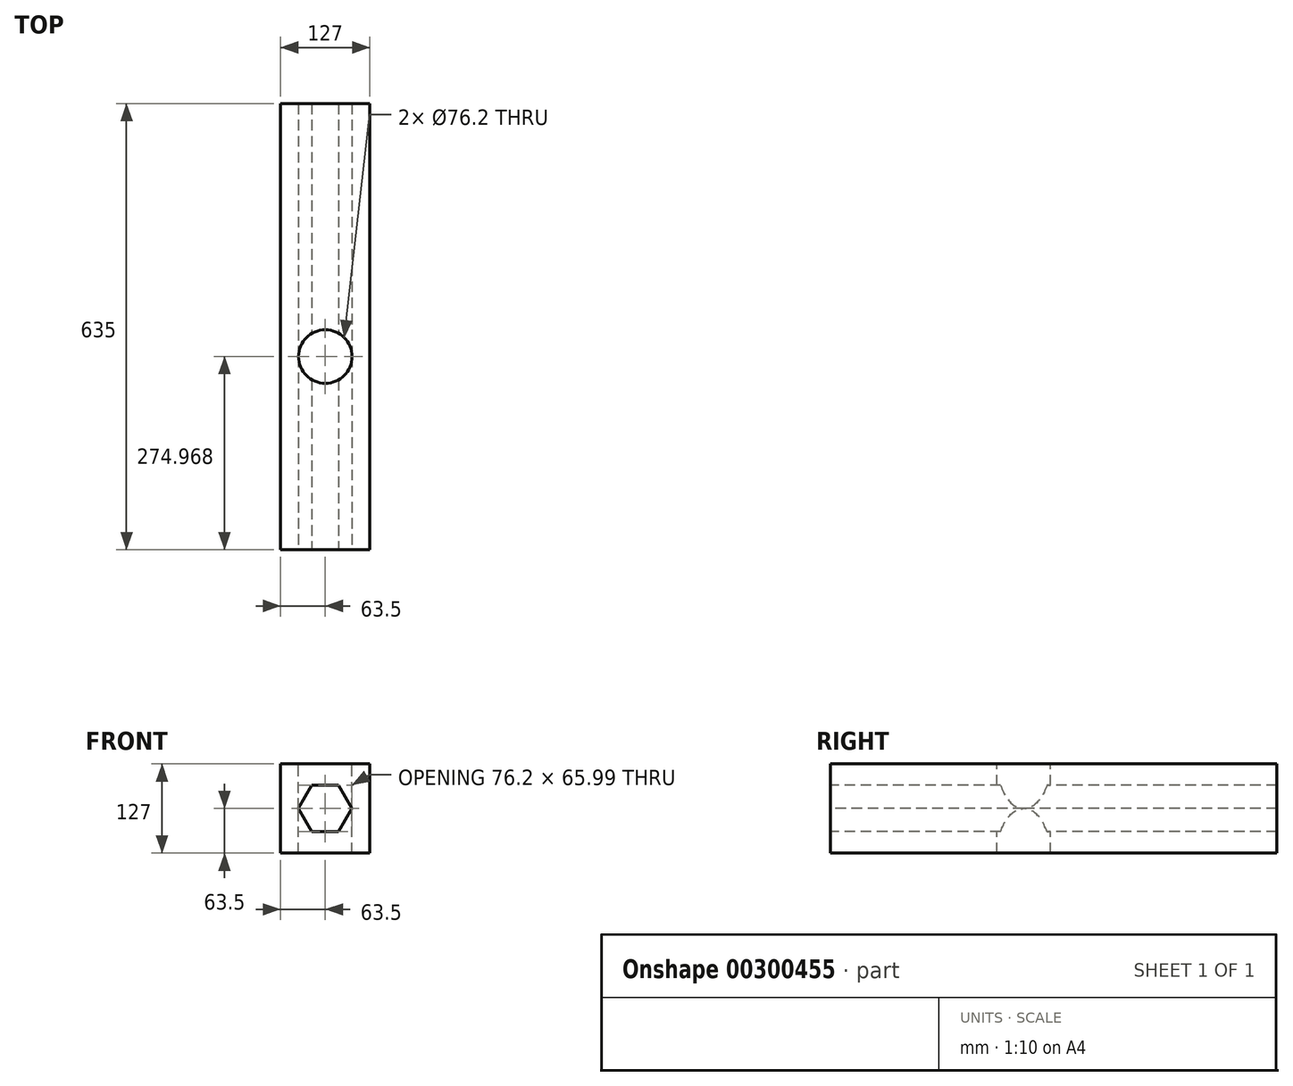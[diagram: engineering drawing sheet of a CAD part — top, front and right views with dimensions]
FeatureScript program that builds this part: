
annotation { "Feature Type Name" : "Feature", "Feature Type Description" : "" }
export const myFeature = defineFeature(function(context is Context, id is Id, definition is map)
    precondition{}
    {
        {
            var Q0;
            Q0=qCreatedBy(makeId("Front.planeOp"),FACE);
            var sketch = newSketch(context, id + "F0", { "sketchPlane" : qUnion([Q0])});
            skLineSegment(sketch, "E0", {"start": v(63.5, 63.5) * mm, "end": v(-63.5, 63.5) * mm});
            skLineSegment(sketch, "E1", {"start": v(-63.5, 63.5) * mm, "end": v(-63.5, -63.5) * mm});
            skLineSegment(sketch, "E2", {"start": v(-63.5, -63.5) * mm, "end": v(63.5, -63.5) * mm});
            skLineSegment(sketch, "E3", {"start": v(63.5, -63.5) * mm, "end": v(63.5, 63.5) * mm});
            skSolve(sketch);
        }
        {
            var Q0;
            Q0 = qSketchRegion(id + "F0", true);
            extrude(context, id + "F1", {"entities" : qUnion([Q0]), "depth" : 635 * mm});
        }
        {
            var Q0;
            Q0=makeQuery(id+"F1.opExtrude","SWEPT_FACE",FACE,{"disambiguationData":[OSD([sQuery(id+"F0.wireOp",EDGE,"E0")])]});
            var sketch = newSketch(context, id + "F2", { "sketchPlane" : qUnion([Q0])});
            skCircle(sketch, "E4", {"center": v(0, -360.03) * mm, "radius": 38.1 * mm});
            skSolve(sketch);
        }
        {
            var Q0;
            Q0 = qSketchRegion(id + "F2", true);
            extrude(context, id + "F3", {"entities" : qUnion([Q0]), "operationType" : NewBodyOperationType.REMOVE, "endBound" : BoundingType.THROUGH_ALL, "oppositeDirection" : true, "depth" : 25.4 * mm});
        }
        {
            var Q0;
            Q0=makeQuery(id+"F1.opExtrude","CAP_FACE",FACE,{"disambiguationData":[OSD([sQuery(id+"F0.wireOp",EDGE,"E0"),sQuery(id+"F0.wireOp",EDGE,"E1"),sQuery(id+"F0.wireOp",EDGE,"E2"),sQuery(id+"F0.wireOp",EDGE,"E3")])],"isStart":false});
            var sketch = newSketch(context, id + "F4", { "sketchPlane" : qUnion([Q0])});
            skCircle(sketch, "E5.cCircle", {"center": v(0, 0) * mm, "radius": 38.1 * mm, "construction": true});
            skLineSegment(sketch, "E5.0", {"start": v(38.1, 0) * mm, "end": v(19.05, -33) * mm});
            skLineSegment(sketch, "E5.1", {"start": v(19.05, -33) * mm, "end": v(-19.05, -33) * mm});
            skLineSegment(sketch, "E5.2", {"start": v(-19.05, -33) * mm, "end": v(-38.1, 0) * mm});
            skLineSegment(sketch, "E5.3", {"start": v(-38.1, 0) * mm, "end": v(-19.05, 33) * mm});
            skLineSegment(sketch, "E5.4", {"start": v(-19.05, 33) * mm, "end": v(19.05, 33) * mm});
            skLineSegment(sketch, "E5.5", {"start": v(19.05, 33) * mm, "end": v(38.1, 0) * mm});
            skSolve(sketch);
        }
        {
            var Q0;
            Q0 = qSketchRegion(id + "F4", true);
            extrude(context, id + "F5", {"entities" : qUnion([Q0]), "operationType" : NewBodyOperationType.REMOVE, "endBound" : BoundingType.THROUGH_ALL, "oppositeDirection" : true, "depth" : 25.4 * mm});
        }
    });
